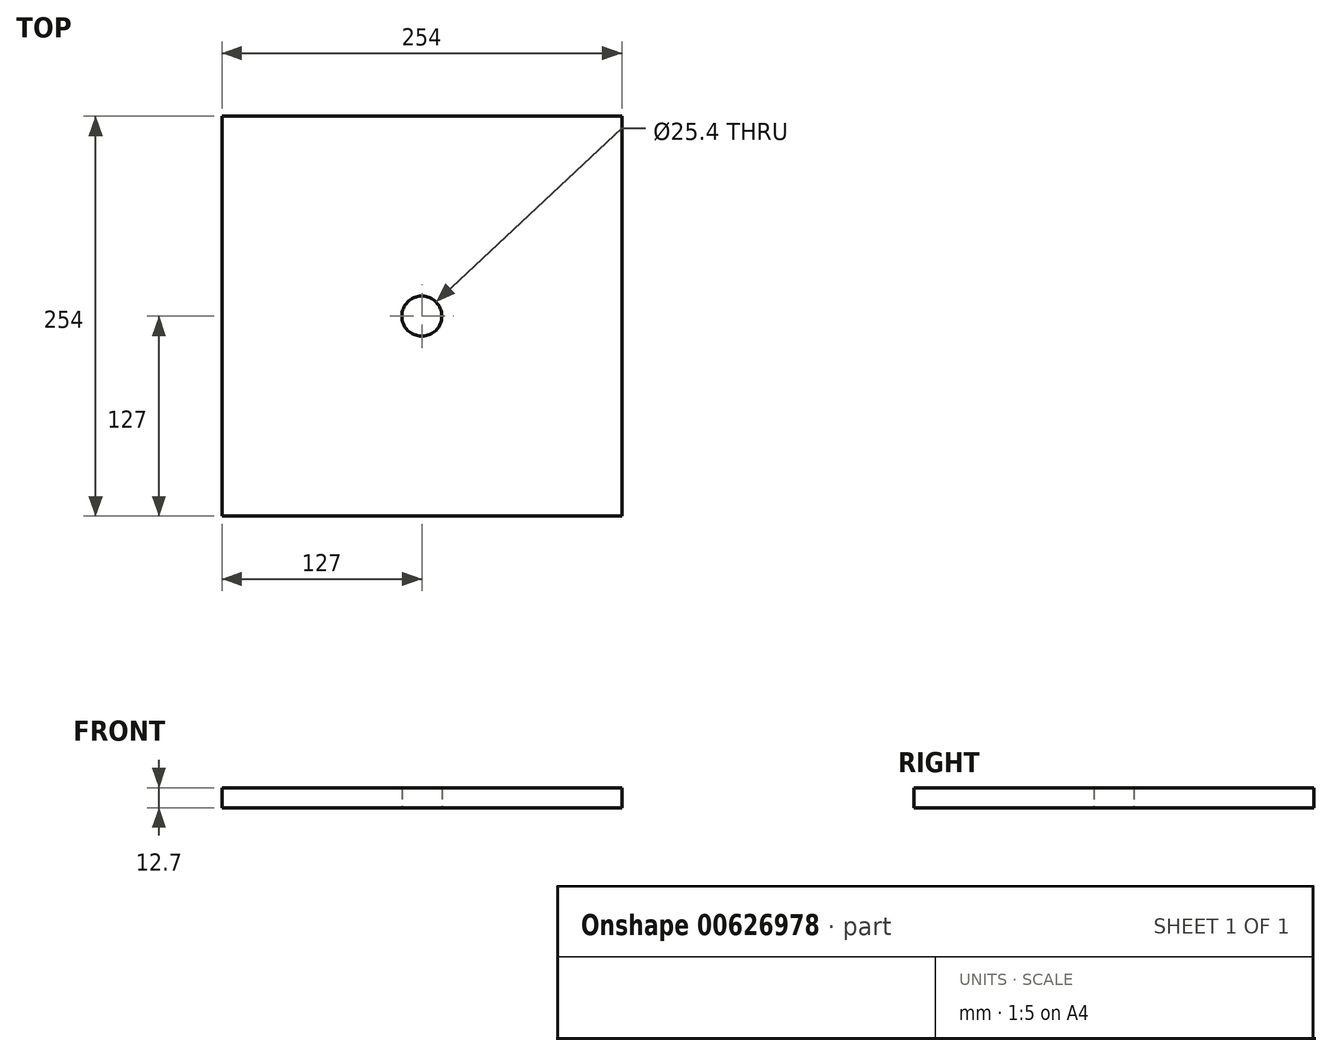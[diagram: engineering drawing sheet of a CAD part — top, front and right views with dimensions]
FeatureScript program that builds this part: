
annotation { "Feature Type Name" : "Feature", "Feature Type Description" : "" }
export const myFeature = defineFeature(function(context is Context, id is Id, definition is map)
    precondition{}
    {
        {
            var Q0;
            Q0=qCreatedBy(makeId("Top.planeOp"),FACE);
            var sketch = newSketch(context, id + "F0", { "sketchPlane" : qUnion([Q0])});
            skLineSegment(sketch, "E0.bottom", {"start": v(127, -127) * mm, "end": v(-127, -127) * mm});
            skLineSegment(sketch, "E0.top", {"start": v(127, 127) * mm, "end": v(-127, 127) * mm});
            skLineSegment(sketch, "E0.left", {"start": v(127, -127) * mm, "end": v(127, 127) * mm});
            skLineSegment(sketch, "E0.right", {"start": v(-127, -127) * mm, "end": v(-127, 127) * mm});
            skPoint(sketch, "E0.middle", {"position": v(0, 0) * mm});
            skCircle(sketch, "E1", {"center": v(0, 0) * mm, "radius": 12.7 * mm});
            skSolve(sketch);
        }
        {
            var Q0;
            Q0 = qSketchRegion(id + "F0", true);
            extrude(context, id + "F1", {"entities" : qUnion([Q0]), "depth" : 12.7 * mm, "offsetDistance" : 25.4 * mm});
        }
    });
